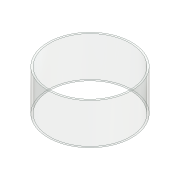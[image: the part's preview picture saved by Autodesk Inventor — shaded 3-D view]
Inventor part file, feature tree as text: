
AUTODESK INVENTOR PART (.ipt)
format: ipt  version: 2018 (Build 220112000, 112)  size: 88,576 bytes
history: native  units: mm
features: extrude x1, sketch x1
ambient origin geometry x8: Origin, YZ Plane, XZ Plane, XY Plane, X Axis, Y Axis, Z Axis, Center Point
bodies: Solid1 (feature_tree)
feature tree (2):
  extrude  "Extrusion1"  [1 undecoded]
  sketch  "Sketch1"  dims[d0=76.2mm d1=79.375mm d2=38.75mm d3=0.0mm]
note: 1 required parameter value undecoded (feature->parameter linkage not recoverable at this tier; creation-order binding heuristic only, values carry confidence <= 0.55)
